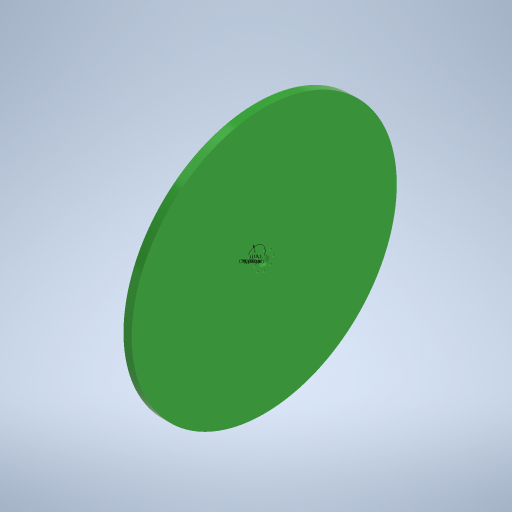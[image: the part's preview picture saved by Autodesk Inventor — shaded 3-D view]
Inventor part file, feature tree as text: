
AUTODESK INVENTOR PART (.ipt)
format: ipt  version: 2024.2 (Build 282272000, 272)  size: 279,040 bytes
history: native  units: mm
features: other x2, sketch x2, extrude x2, revolve x1, fillet x1
ambient origin geometry x8: Origin, YZ Plane, XZ Plane, XY Plane, X Axis, Y Axis, Z Axis, Center Point
bodies: Body1 (feature_tree)
feature tree (8):
  other  "Bryła1"
  revolve  "Obrót1"
  sketch  "Szkic2"
  extrude  "Wyciągnięcie proste1"  Depth=6.0mm
  extrude  "Wyciągnięcie proste2"  Depth=4.1mm
  fillet  "Zaokrąglenie1"  Radius=1.0mm
  sketch  "Szkic1"
  other  "Finish1"
